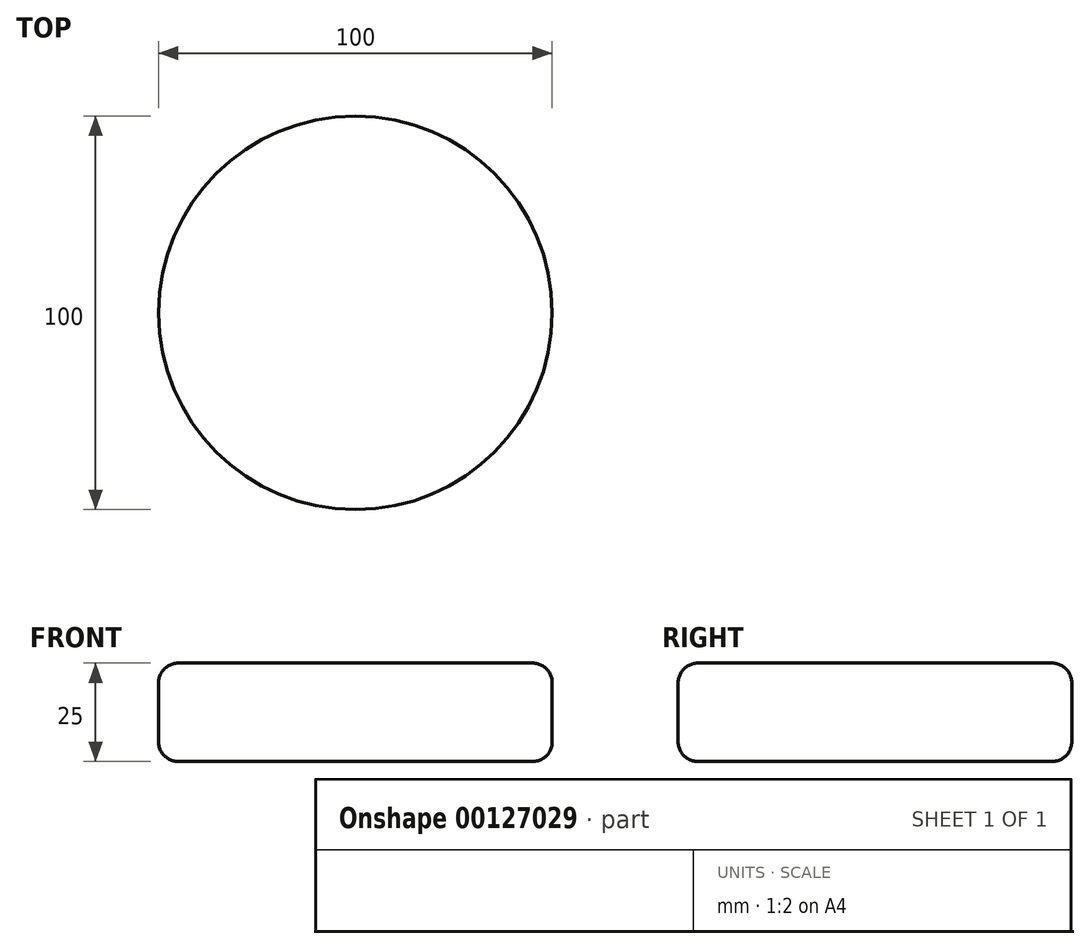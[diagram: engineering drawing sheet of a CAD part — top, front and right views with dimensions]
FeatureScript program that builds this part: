
annotation { "Feature Type Name" : "Feature", "Feature Type Description" : "" }
export const myFeature = defineFeature(function(context is Context, id is Id, definition is map)
    precondition{}
    {
        {
            var Q0;
            Q0=qCreatedBy(makeId("Top.planeOp"),FACE);
            var sketch = newSketch(context, id + "F0", { "sketchPlane" : qUnion([Q0])});
            skCircle(sketch, "E0", {"center": v(0, 0) * mm, "radius": 50 * mm});
            skSolve(sketch);
        }
        {
            var Q0;
            Q0 = qSketchRegion(id + "F0", true);
            extrude(context, id + "F1", {"entities" : qUnion([Q0]), "depth" : 25 * mm});
        }
        {
            var Q0;
            Q0=makeQuery(id+"F1.opExtrude","CAP_EDGE",EDGE,{"disambiguationData":[OSD([sQuery(id+"F0.wireOp",EDGE,"E0")])],"isStart":false});
            var Q1;
            Q1=makeQuery(id+"F1.opExtrude","CAP_FACE",FACE,{"disambiguationData":[OSD([sQuery(id+"F0.wireOp",EDGE,"E0")])],"isStart":true});
            fillet(context, id + "F2", {"entities" : qUnion([Q0, Q1]), "radius" : 5 * mm, "tangentPropagation" : true, "allowEdgeOverflow" : false});
        }
    });
